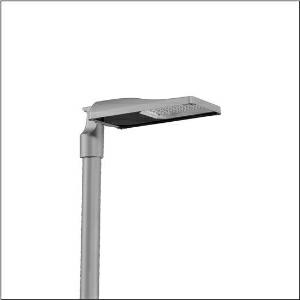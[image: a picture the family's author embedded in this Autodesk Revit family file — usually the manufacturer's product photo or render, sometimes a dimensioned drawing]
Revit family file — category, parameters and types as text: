
# Revit family: streetlight_sl_31_mini___st1_0a_5xh2d71b08ga_5698
name_source: partatom
category: Lighting Fixtures
units: mm (PartAtom-declared; Revit-internal decimal feet)

## family parameters
Cut with Voids When Loaded = No
Host = Face
Light Source = No
Part Type = Normal
Room Calculation Point = No
Round Connector Dimension = Use Diameter
Shared = No

## types (1)
- --- (1 x LED, 4620 lm, 37.3 W, 2200K)
    Apparent Load = 37 VA
    CIE Flux Codes = 37 72 97 100 100
    Color Rendering = 70
    Color Temperature = 2200K
    Default Elevation = 1800 mm
    Description = Streetlight SL 31 mini Easy, LST, Desk-Remote mast luminaire for post-top, side-entry; light control with lens of PMMA; light distribution: ST1.0a, direct asymmetric distribution, for standard-compliant lighting for roads and squares; LED: luminous flux: 4.620lm, light colour: 722, colour temperature: 2200K; luminous efficacy: 123,9lm/W; control: pre-setting: linear dimming characteristic, flexible luminous flux parameterisation, time-dependent luminous flux control, constant luminous flux control, power reduction, intelligent temperature release in ECG and LED module, overheat protection; luminaire housing, of diecast aluminium, Siteco® metallic grey (DB 702S), corrosivity category C5 high according to DIN EN ISO 12944; cover of toughened safety glass, transparent, mast flange of diecast aluminium, Siteco® metallic grey (DB 702S), spigot size: 76/60mm, mast flange included unmounted; with cable H07RN-F 3x 1.5mm², cable length: 6,5m, connection cable pre-assembled; mains connection: 220..240V, AC, 50/60Hz; power consumption (at start of service life): 37,3W / (at end of service life): 38,7W / (with reduced operation 50%): 17,3W; protection rating (complete): IP66; insulation class (complete): insulation class II (safety insulation); impact resistance: IK10; certification: CE, ENEC, ENEC+, VDE, UKCA; permissible operating ambient temperature for outdoor applications: -40..+50°C; packaging unit: 1 piece

Light Distribution: ST1.0a
    Height = 76 mm
    Lamp = 1 x LED
    Lamp Light Flux = 4620 lm
    Lamp Power = 37.3 W
    Lamp count = 1
    Length = 547 mm
    Luminous efficacy = 124 lm/W
    Manufacturer = Siteco
    ModVariant = No
    Model = 5XH2D71B08GA
    Number of Poles = 1
    OnlyDefault = Yes
    Power Factor = 1
    Product Name = Streetlight SL 31 mini | ST1.0a
    Product group = mast luminaire | pylon top
    ProductGroupID = 6100
    Protection Class = Protection class II
    Protection Degree = IP 66
    RLX_Detail_Level = 1
    RLX_Emergency_Light_Flux = 0 lm
    RLX_Emergency_Type = 0
    RLX_Emergency_Type_DB = No
    RlxData = <blob elided: 39609 chars, md5=fead02fa>
    Socket = socket
    Standby Power = 0 W
    System Light Flux = 4620 lm
    System Power = 37 W
    Type Comments = factory setting: luminous flux: 100 % | dim-lin: 254 | 386 mA
    Type Image = l_1300326.jpg
    URL = http://relux.com
    VarID = @adj_008821
    Voltage = 0 V
    Weight = 0.00 kg
    Width = 265 mm

## geometry (parser evidence)
native form markers: Blend x4, Sweep x9
no freeform markers — native parametric forms only
